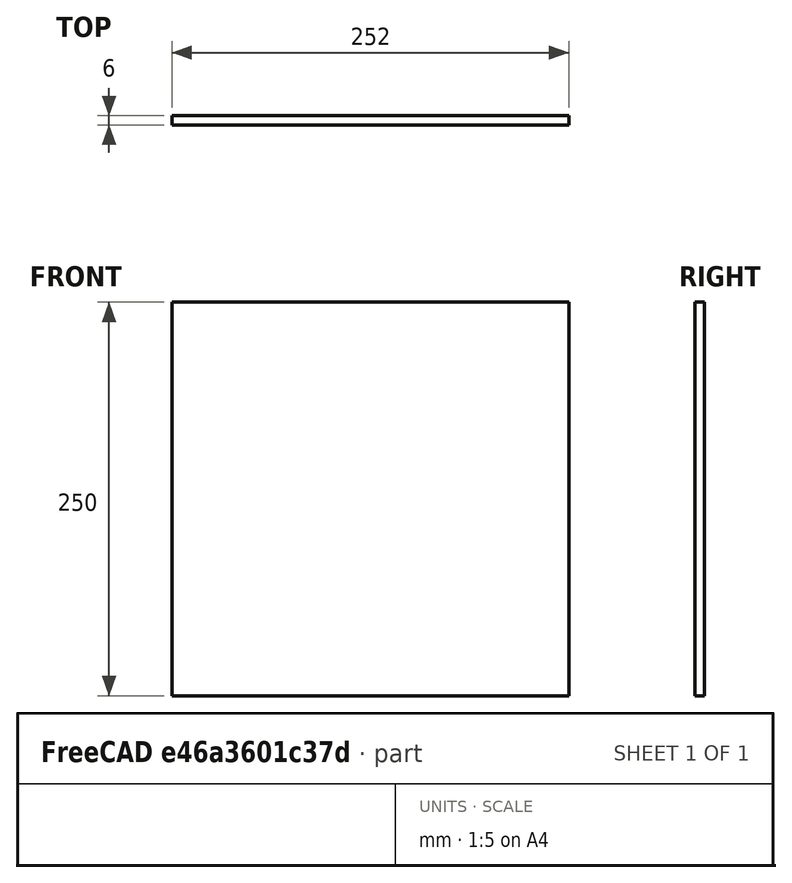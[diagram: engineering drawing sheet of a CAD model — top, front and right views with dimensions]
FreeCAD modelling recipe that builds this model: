
FCSTD DOCUMENT  (FreeCAD 0.18R4 (GitTag))
Label: Gabinete_Front
License: All rights reserved
LicenseURL: http://en.wikipedia.org/wiki/All_rights_reserved
objects: Sketcher::SketchObject×1, PartDesign::Pad×1, PartDesign::Body×1
note: 4 computed .brp shape members not serialized (recipe doc carries the construction recipe); baked Part::Feature solids carry a one-line shape summary decoded from their .brp

FEATURE [Sketcher::SketchObject] Sketch
  MapMode = 5
  Placement = pos=(0,0,0) rot=(1,0,0;1.5708rad)
  Support = -> [XZ_Plane]
  sketch-geometry (4):
    g0: LineSegment StartX=0 StartY=0 StartZ=0 EndX=252 EndY=0 EndZ=0
    g1: LineSegment StartX=252 StartY=0 StartZ=0 EndX=252 EndY=250 EndZ=0
    g2: LineSegment StartX=252 StartY=250 StartZ=0 EndX=0 EndY=250 EndZ=0
    g3: LineSegment StartX=0 StartY=250 StartZ=0 EndX=0 EndY=0 EndZ=0
  constraints (11):
    c: Coincident(g0,g1)
    c: Coincident(g1,g2)
    c: Coincident(g2,g3)
    c: Coincident(g3,g0)
    c: Horizontal(g0)
    c: Horizontal(g2)
    c: Vertical(g1)
    c: Vertical(g3)
    c: Coincident(g0,g-1)
    c: DistanceX(g0,g0) = 252
    c: DistanceY(g3,g3) = 250
FEATURE [PartDesign::Pad] Pad
  Length = 6
  Length2 = 100
  Placement = pos=(0,0,0) rot=(1,0,0;1.5708rad)
  Profile = -> Sketch
  Type = 0
FEATURE [PartDesign::Body] Body
  Group = -> [Sketch,Pad]
  Origin = -> Origin
  Tip = -> Pad
